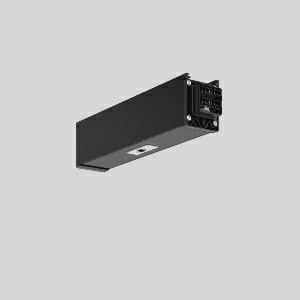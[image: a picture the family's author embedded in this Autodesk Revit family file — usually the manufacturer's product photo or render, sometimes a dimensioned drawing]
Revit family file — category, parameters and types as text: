
# Revit family: linedo_sensormodule_2-5_m_9503s1_003_400_000_ef30
name_source: partatom
category: Lighting Fixtures
units: mm (PartAtom-declared; Revit-internal decimal feet)

## family parameters
Cut with Voids When Loaded = No
Host = Face
Light Source = No
Part Type = Normal
Room Calculation Point = No
Round Connector Dimension = Use Diameter
Shared = No

## types (1)
- LINEDO Sensormodule 2-5 m
    Apparent Load = 0 VA
    Default Elevation = 1800 mm
    Description = Series: LINEDO
Module including Passive Infrared (PIR) sensor for movement and ambient light. System profile made of aluminium extrusion profile, powder-coated. Simple, tool-free installation of system profiles using separate accessories for cable, chain or ceiling suspension. Tool-free connection and mechanical connectors to secure. 14-poles LINEDO connector (5 x 2.5 mm² / 9 x 1.5 mm²) for additional applications in light management or for the integration of emergency lighting. Phase can be set via patended bridge without opening the luminaire. Pre-assembled connector for DALI line. Light and movement sensor: Housing of non-flammable, halogen-free plastic (polycarbonate). Presence detection with passive IR element. Presence detection range adjustable via integrated shutters between 40° and 90°. Detection range: 6 m. Light sensor range: 20-800 lx (measured at the sensor). Function display with two-colour LED. Installation height: 2-5 m. Example of use: Monitoring of low ceiling rooms and rack storage where the installation height is normal. Please order supply module, connection and mounting accessories separately. 
Colour: jet black (RAL 9005)
Length: 330 mm
Width: 58 mm
Height: 76 mm
Weight: 770 g
Type of Installation: Surface mounting
    Height = 77 mm
    Lamp = 0 x
    Length = 331 mm
    Luminous efficacy = 0 lm/W
    Manufacturer = RZB
    ModVariant = No
    Model = 9503S1.003.400.000
    Mounting Place = Ceiling
    Mounting Type = Surface mounted, Pendant
    Number of Poles = 1
    OnlyDefault = Yes
    Power Factor = 1
    Product Name = LINEDO Sensormodule 2-5 m
    Product group = Surface mounted continuous line luminaire system
    ProductGroupID = 310
    Protection Class = Protection class I
    Protection Degree = IP 20
    RLX_Detail_Level = 1
    RLX_Emergency_Light_Flux = 0 lm
    RLX_Emergency_Type = 0
    RLX_Emergency_Type_DB = No
    RlxData = <blob elided: 24485 chars, md5=a1698f45>
    Standby Power = 0 W
    System Light Flux = 0 lm
    System Power = 0 W
    Type Comments = Product without accessories
    Type Image = 9503s1.003.400.000.jpg
    URL = http://relux.com
    VarID = ---
    Voltage = 230 V
    Voltage Range = 220-240 V
    Weight = 0.00 kg
    Width = 58 mm

## geometry (parser evidence)
native form markers: Blend x4, Sweep x10
no freeform markers — native parametric forms only
